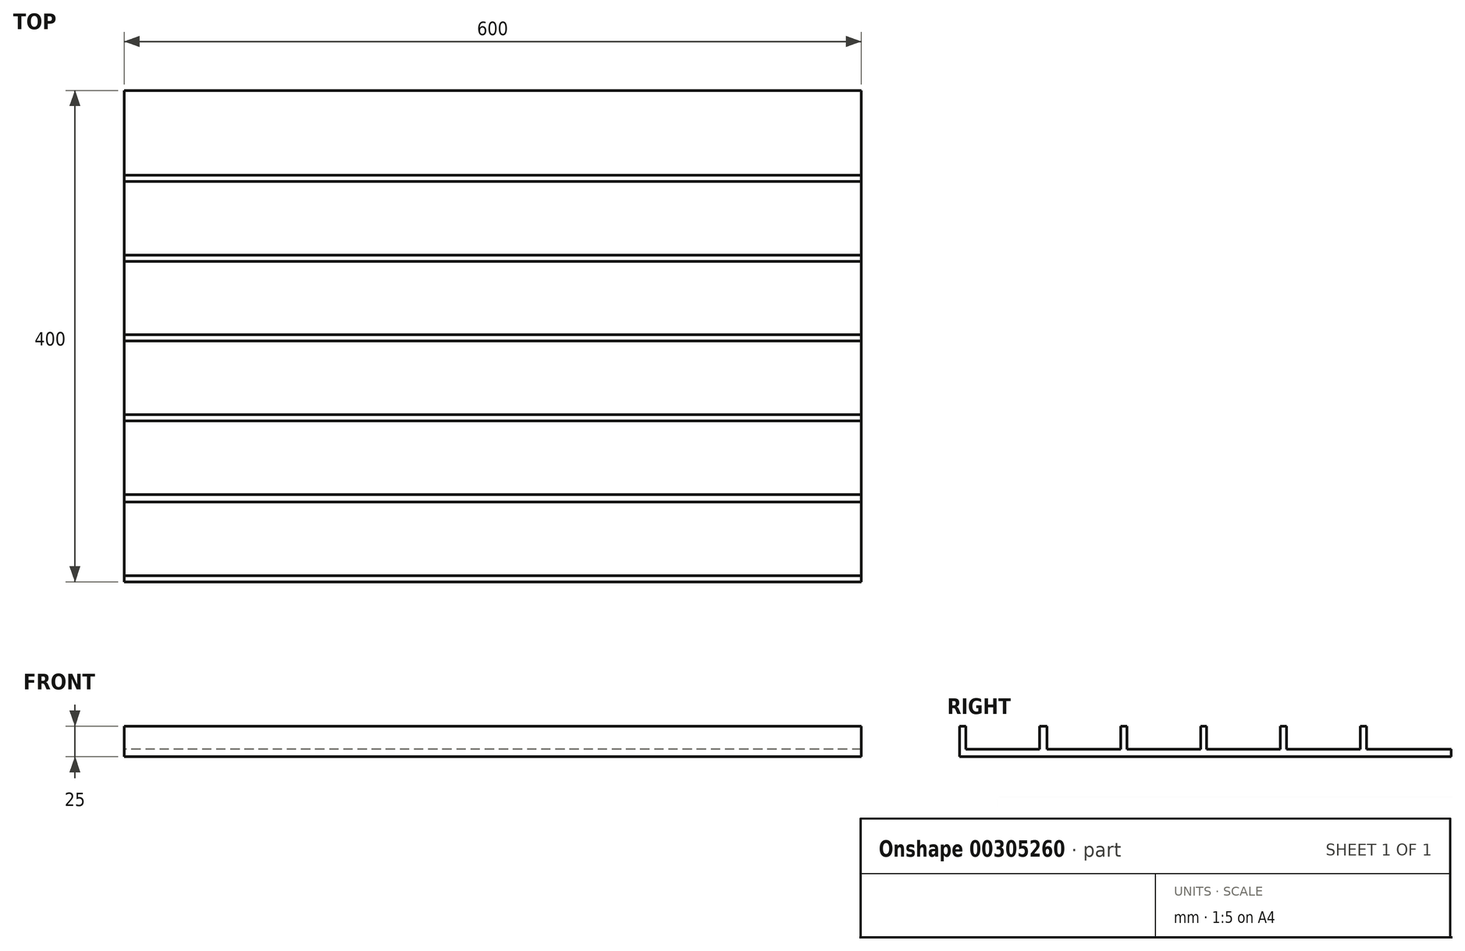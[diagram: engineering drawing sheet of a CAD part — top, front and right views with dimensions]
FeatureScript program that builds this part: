
annotation { "Feature Type Name" : "Feature", "Feature Type Description" : "" }
export const myFeature = defineFeature(function(context is Context, id is Id, definition is map)
    precondition{}
    {
        {
            var Q0;
            Q0=qCreatedBy(makeId("Top.planeOp"),FACE);
            var sketch = newSketch(context, id + "F0", { "sketchPlane" : qUnion([Q0])});
            skLineSegment(sketch, "E0.bottom", {"start": v(300, -200) * mm, "end": v(-300, -200) * mm});
            skLineSegment(sketch, "E0.top", {"start": v(300, 200) * mm, "end": v(-300, 200) * mm});
            skLineSegment(sketch, "E0.left", {"start": v(300, -200) * mm, "end": v(300, 200) * mm});
            skLineSegment(sketch, "E0.right", {"start": v(-300, -200) * mm, "end": v(-300, 200) * mm});
            skPoint(sketch, "E0.middle", {"position": v(0, 0) * mm});
            skSolve(sketch);
        }
        {
            var Q0;
            Q0 = qSketchRegion(id + "F0", true);
            extrude(context, id + "F1", {"entities" : qUnion([Q0]), "depth" : 6 * mm});
        }
        {
            var Q0;
            Q0=qCreatedBy(makeId("Top.planeOp"),FACE);
            var sketch = newSketch(context, id + "F2", { "sketchPlane" : qUnion([Q0])});
            skLineSegment(sketch, "E1.bottom", {"start": v(-300, -135) * mm, "end": v(300, -135) * mm});
            skLineSegment(sketch, "E1.top", {"start": v(-300, -129) * mm, "end": v(300, -129) * mm});
            skLineSegment(sketch, "E1.left", {"start": v(-300, -135) * mm, "end": v(-300, -129) * mm});
            skLineSegment(sketch, "E1.right", {"start": v(300, -135) * mm, "end": v(300, -129) * mm});
            skLineSegment(sketch, "E2.bottom", {"start": v(-300, -69) * mm, "end": v(300, -69) * mm});
            skLineSegment(sketch, "E2.top", {"start": v(-300, -64) * mm, "end": v(300, -64) * mm});
            skLineSegment(sketch, "E2.left", {"start": v(-300, -69) * mm, "end": v(-300, -64) * mm});
            skLineSegment(sketch, "E2.right", {"start": v(300, -69) * mm, "end": v(300, -64) * mm});
            skLineSegment(sketch, "E3.bottom", {"start": v(-300, -4) * mm, "end": v(300, -4) * mm});
            skLineSegment(sketch, "E3.top", {"start": v(-300, 1) * mm, "end": v(300, 1) * mm});
            skLineSegment(sketch, "E3.left", {"start": v(-300, -4) * mm, "end": v(-300, 1) * mm});
            skLineSegment(sketch, "E3.right", {"start": v(300, -4) * mm, "end": v(300, 1) * mm});
            skLineSegment(sketch, "E4.bottom", {"start": v(-300, 61) * mm, "end": v(300, 61) * mm});
            skLineSegment(sketch, "E4.top", {"start": v(-300, 66) * mm, "end": v(300, 66) * mm});
            skLineSegment(sketch, "E4.left", {"start": v(-300, 61) * mm, "end": v(-300, 66) * mm});
            skLineSegment(sketch, "E4.right", {"start": v(300, 61) * mm, "end": v(300, 66) * mm});
            skLineSegment(sketch, "E5.bottom", {"start": v(-300, 126) * mm, "end": v(300, 126) * mm});
            skLineSegment(sketch, "E5.top", {"start": v(-300, 131) * mm, "end": v(300, 131) * mm});
            skLineSegment(sketch, "E5.left", {"start": v(-300, 126) * mm, "end": v(-300, 131) * mm});
            skLineSegment(sketch, "E5.right", {"start": v(300, 126) * mm, "end": v(300, 131) * mm});
            skLineSegment(sketch, "E6.bottom", {"start": v(-300, -195) * mm, "end": v(300, -195) * mm});
            skLineSegment(sketch, "E6.top", {"start": v(-300, -200) * mm, "end": v(300, -200) * mm});
            skLineSegment(sketch, "E6.left", {"start": v(-300, -195) * mm, "end": v(-300, -200) * mm});
            skLineSegment(sketch, "E6.right", {"start": v(300, -195) * mm, "end": v(300, -200) * mm});
            skSolve(sketch);
        }
        {
            var Q0;
            Q0 = qSketchRegion(id + "F2", true);
            extrude(context, id + "F3", {"entities" : qUnion([Q0]), "operationType" : NewBodyOperationType.ADD, "depth" : 25 * mm});
        }
    });
